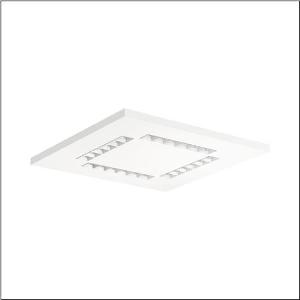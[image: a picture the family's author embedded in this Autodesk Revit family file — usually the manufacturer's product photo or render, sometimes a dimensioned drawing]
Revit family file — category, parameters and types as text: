
# Revit family: silica_21_square_51mx6nds44w
name_source: partatom
category: Lighting Fixtures
units: mm (PartAtom-declared; Revit-internal decimal feet)

## family parameters
Cut with Voids When Loaded = No
Host = Face
Light Source = No
Part Type = Normal
Room Calculation Point = No
Round Connector Dimension = Use Diameter
Shared = No

## types (1)
- --- (1 x LED, 4600 lm, 27 W, 4000K)
    Apparent Load = 27 VA
    CIE Flux Codes = 83 98 100 100 100
    Color Rendering = 80
    Color Temperature = 4000K
    Default Elevation = 1800 mm
    Description = Silica 21 Square, office luminaire, primary light control with lens, of PMMA, primary anti-glare with reflector, of PC, white, CAT 2 (L<= 3000cd/m²), light emission: direct distribution, primary light characteristic: symmetric, installation type: lay-in mounting, LED, rated luminous flux: 4.600lm, luminous efficacy: 170lm/W, light colour: 840, colour temperature: 4000K, control gear: DALI 2, with terminal, 5-pole, mains connection: 220..240V, AC, 50/60Hz, rated input power: 27W, luminaire housing, of aluminium, traffic white (RAL 9016), module: M600, length: 600mm, width: 600mm, height: 32mm, protection rating (complete): IP20, insulation class (complete): insulation class I (protective earthing), certification: CE, ENEC, VDE, permissible operating ambient temperature: 0..+35°C, standard: EN 50419, packaging unit: 1 piece
    Height = 0 mm  [stored 0 ft]
    Lamp = 1 x LED
    Lamp Light Flux = 4600 lm
    Lamp Power = 27 W
    Lamp count = 1
    Length = 597 mm
    Luminous efficacy = 170 lm/W
    Manufacturer = Siteco
    ModVariant = No
    Model = 51MX6NDS44W
    Mounting Place = Ceiling
    Mounting Type = Recessed
    Number of Poles = 1
    OnlyDefault = Yes
    Power Factor = 1
    Product Name = Silica 21 Square
    Product group = office luminaire | ceiling recessed
    ProductGroupID = 400
    Protection Class = Protection class I
    Protection Degree = IP 20
    RLX_Detail_Level = 1
    RLX_Emergency_Light_Flux = 0 lm
    RLX_Emergency_Type = 0
    RLX_Emergency_Type_DB = No
    RlxData = <blob elided: 18981 chars, md5=989510fa>
    Socket = socket
    Standby Power = 0 W
    System Light Flux = 4600 lm
    System Power = 27 W
    Type Comments = factory setting: luminous flux: 100 % | dim-lin: 254 | 366 mA
    Type Image = l_1275224.jpg
    URL = http://relux.com
    VarID = @adj_090005
    Voltage = 0 V
    Weight = 0.00 kg
    Width = 597 mm

note: [stored X ft] marks values corroborated as IEEE doubles in the binary element streams (Revit-internal decimal feet)

## geometry (parser evidence)
native form markers: Blend x4, Sweep x11
no freeform markers — native parametric forms only
